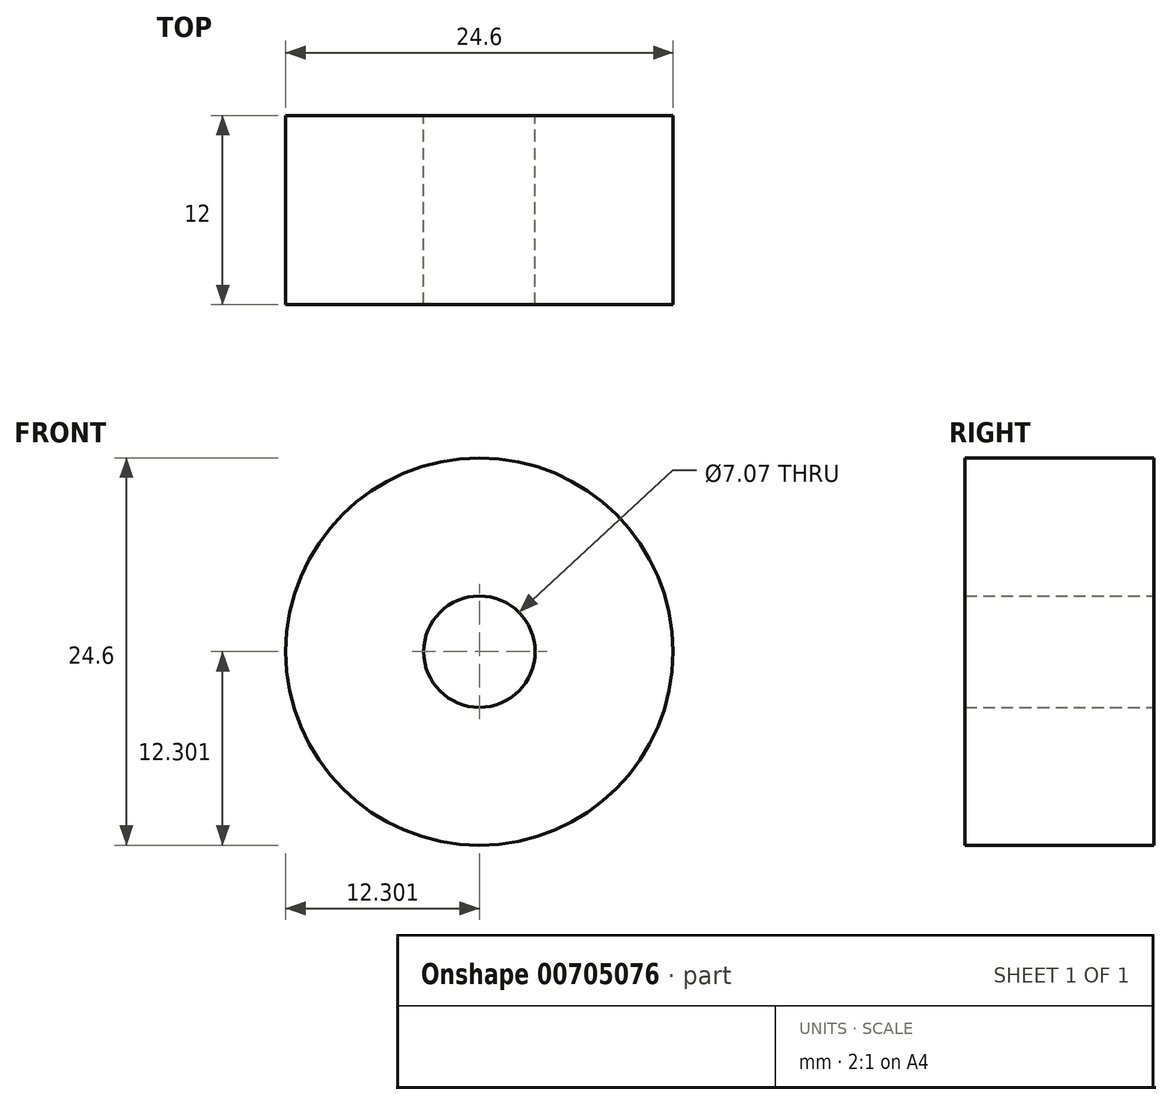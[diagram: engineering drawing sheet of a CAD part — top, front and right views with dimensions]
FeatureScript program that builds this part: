
annotation { "Feature Type Name" : "Feature", "Feature Type Description" : "" }
export const myFeature = defineFeature(function(context is Context, id is Id, definition is map)
    precondition{}
    {
        {
            var Q0;
            Q0=qCreatedBy(makeId("Front.planeOp"),FACE);
            var sketch = newSketch(context, id + "F0", { "sketchPlane" : qUnion([Q0])});
            skCircle(sketch, "E0", {"center": v(-37.99, 42.02) * mm, "radius": 12.3 * mm});
            skCircle(sketch, "E1", {"center": v(-37.99, 42.02) * mm, "radius": 3.54 * mm});
            skSolve(sketch);
        }
        {
            var Q0;
            Q0 = qSketchRegion(id + "F0", true);
            extrude(context, id + "F1", {"entities" : qUnion([Q0]), "depth" : 10 * mm, "offsetDistance" : 25.4 * mm, "hasSecondDirection" : true, "secondDirectionOppositeDirection" : true, "secondDirectionDepth" : 2 * mm});
        }
    });
